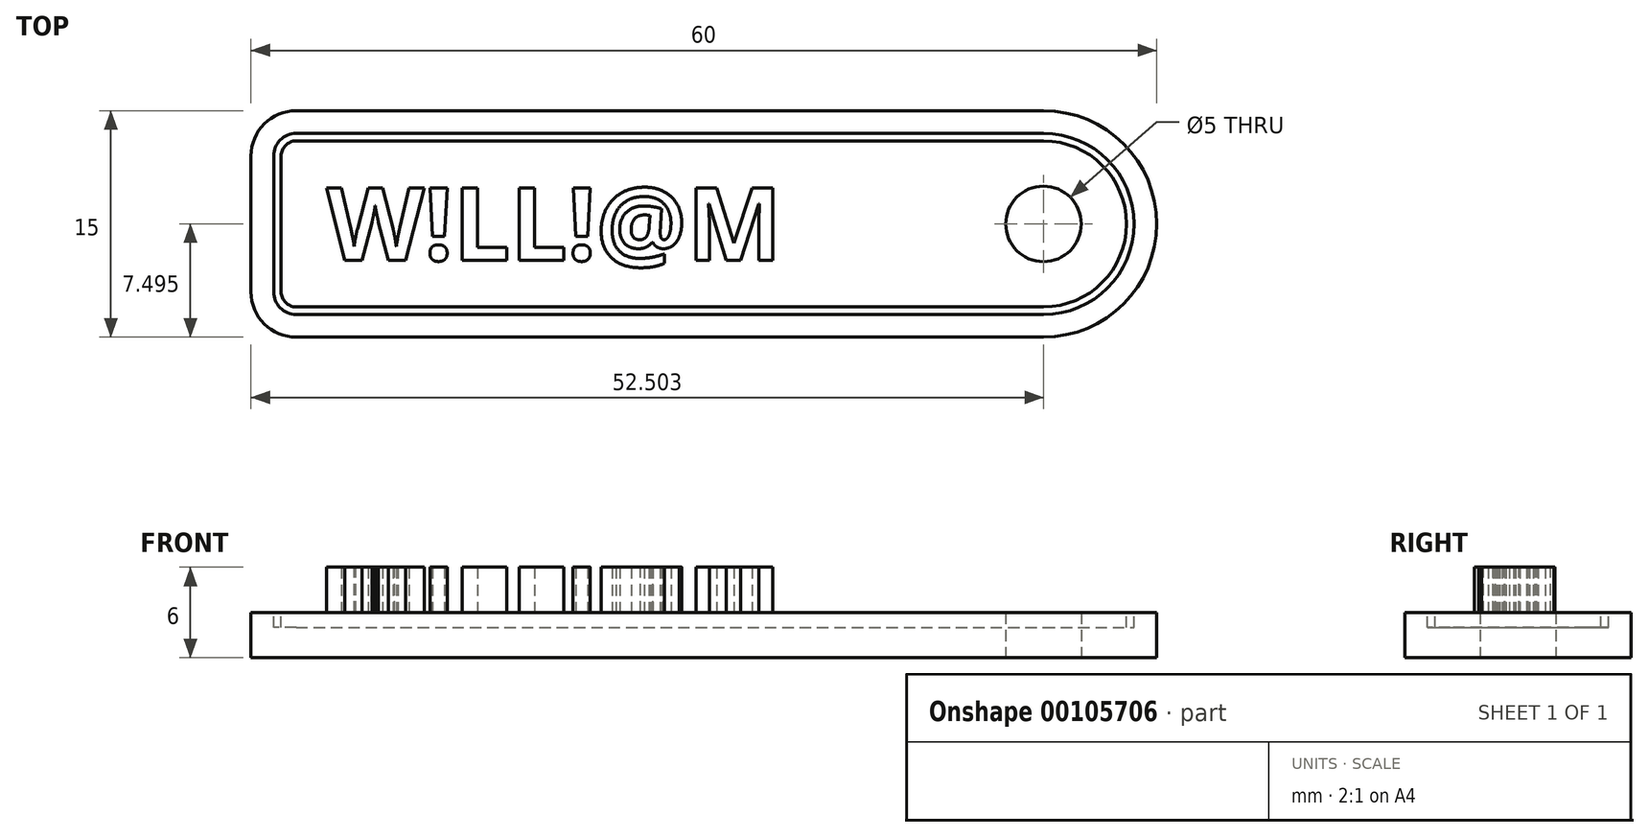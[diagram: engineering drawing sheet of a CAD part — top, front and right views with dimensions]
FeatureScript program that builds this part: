
annotation { "Feature Type Name" : "Feature", "Feature Type Description" : "" }
export const myFeature = defineFeature(function(context is Context, id is Id, definition is map)
    precondition{}
    {
        {
            var Q0;
            Q0=qCreatedBy(makeId("Top.planeOp"),FACE);
            var sketch = newSketch(context, id + "F0", { "sketchPlane" : qUnion([Q0])});
            skLineSegment(sketch, "E0.bottom", {"start": v(-1.37, 15.2) * mm, "end": v(48.13, 15.2) * mm});
            skLineSegment(sketch, "E0.top", {"start": v(-1.37, 0.2) * mm, "end": v(48.13, 0.2) * mm});
            skLineSegment(sketch, "E0.left", {"start": v(-4.37, 12.2) * mm, "end": v(-4.37, 3.2) * mm});
            skPoint(sketch, "E1.visualSharp", {"position": v(-4.37, 15.2) * mm});
            skArc(sketch, "E1.filletArc", {"start": v(-1.37, 15.2) * mm, "mid": v(-3.49, 14.32) * mm, "end": v(-4.37, 12.2) * mm});
            skPoint(sketch, "E2.visualSharp", {"position": v(-4.37, 0.2) * mm});
            skArc(sketch, "E2.filletArc", {"start": v(-4.37, 3.2) * mm, "mid": v(-3.49, 1.07) * mm, "end": v(-1.37, 0.2) * mm});
            skPoint(sketch, "E3.visualSharp", {"position": v(51.13, 0.2) * mm});
            skPoint(sketch, "E4.visualSharp", {"position": v(51.13, 15.2) * mm});
            skArc(sketch, "E5", {"start": v(48.13, 15.2) * mm, "mid": v(55.63, 7.7) * mm, "end": v(48.13, 0.2) * mm});
            skCircle(sketch, "E6", {"center": v(48.13, 7.7) * mm, "radius": 2.5 * mm});
            skSolve(sketch);
        }
        {
            var Q0;
            Q0=makeQuery(id+"F0.imprint","IMPRINT",FACE,{"disambiguationData":[TD([[makeQuery(id+"F0.imprint","IMPRINT",EDGE,{"derivedFrom":sQuery(id+"F0.wireOp",EDGE,"E0.bottom")}),-1.0]])]});
            extrude(context, id + "F1", {"entities" : qUnion([Q0]), "depth" : 3 * mm});
        }
        {
            var Q0;
            Q0=makeQuery(id+"F1.opExtrude","CAP_FACE",FACE,{"disambiguationData":[OSD([sQuery(id+"F0.wireOp",EDGE,"E0.bottom"),sQuery(id+"F0.wireOp",EDGE,"E0.top"),sQuery(id+"F0.wireOp",EDGE,"E0.left"),sQuery(id+"F0.wireOp",EDGE,"E1.filletArc"),sQuery(id+"F0.wireOp",EDGE,"E2.filletArc"),sQuery(id+"F0.wireOp",EDGE,"E5"),sQuery(id+"F0.wireOp",EDGE,"E6")])],"isStart":false});
            var sketch = newSketch(context, id + "F2", { "sketchPlane" : qUnion([Q0])});
            skText(sketch, "E7", { "text": "W!LL!@M", "fontName": "OpenSans-Bold.ttf"});
            skLineSegment(sketch, "E8", {"start": v(55.63, 7.7) * mm, "end": v(-4.37, 7.7) * mm, "construction": true});
            const initialGuessF2  = {"E7": [0.00063, 0.00529, 1, 0, 0.00482]};
            skSetInitialGuess(sketch, initialGuessF2);
            skSolve(sketch);
        }
        {
            var Q0;
            Q0 = qSketchRegion(id + "F2", true);
            extrude(context, id + "F3", {"entities" : qUnion([Q0]), "operationType" : NewBodyOperationType.ADD, "depth" : 3 * mm});
        }
        {
            var Q0;
            {var subQ0=sQuery(id+"F0.wireOp",EDGE,"E6");var subQ1=sQuery(id+"F0.wireOp",EDGE,"E0.left");var subQ2=sQuery(id+"F0.wireOp",EDGE,"E5");var subQ3=sQuery(id+"F0.wireOp",EDGE,"E0.bottom");var subQ4=sQuery(id+"F0.wireOp",EDGE,"E1.filletArc");var subQ5=sQuery(id+"F0.wireOp",EDGE,"E0.top");var subQ6=sQuery(id+"F0.wireOp",EDGE,"E2.filletArc");Q0=makeQuery(id+"F3.boolean.opBoolean","SPLIT",FACE,{"disambiguationData":[TD([makeQuery(id+"F1.opExtrude","SWEPT_FACE",FACE,{"disambiguationData":[OSD([subQ3])]})])],"derivedFrom":makeQuery(id+"F1.opExtrude","CAP_FACE",FACE,{"disambiguationData":[OSD([subQ3,subQ5,subQ1,subQ4,subQ6,subQ2,subQ0])],"isStart":false})});}
            var sketch = newSketch(context, id + "F4", { "sketchPlane" : qUnion([Q0])});
            skArc(sketch, "E9.0", {"start": v(-1.37, 13.7) * mm, "mid": v(-2.43, 13.26) * mm, "end": v(-2.87, 12.2) * mm});
            skArc(sketch, "E9.1", {"start": v(48.13, 13.7) * mm, "mid": v(54.13, 7.7) * mm, "end": v(48.13, 1.7) * mm});
            skLineSegment(sketch, "E9.2", {"start": v(-1.37, 1.7) * mm, "end": v(48.13, 1.7) * mm});
            skLineSegment(sketch, "E9.3", {"start": v(-1.37, 13.7) * mm, "end": v(48.13, 13.7) * mm});
            skArc(sketch, "E9.4", {"start": v(-2.87, 3.2) * mm, "mid": v(-2.43, 2.13) * mm, "end": v(-1.37, 1.7) * mm});
            skLineSegment(sketch, "E9.5", {"start": v(-2.87, 12.2) * mm, "end": v(-2.87, 3.2) * mm});
            skArc(sketch, "E10.0", {"start": v(-1.37, 13.2) * mm, "mid": v(-2.07, 12.9) * mm, "end": v(-2.37, 12.2) * mm});
            skArc(sketch, "E10.1", {"start": v(48.13, 13.2) * mm, "mid": v(53.63, 7.7) * mm, "end": v(48.13, 2.2) * mm});
            skLineSegment(sketch, "E10.2", {"start": v(-1.37, 2.2) * mm, "end": v(48.13, 2.2) * mm});
            skLineSegment(sketch, "E10.3", {"start": v(-1.37, 13.2) * mm, "end": v(48.13, 13.2) * mm});
            skArc(sketch, "E10.4", {"start": v(-2.37, 3.2) * mm, "mid": v(-2.07, 2.49) * mm, "end": v(-1.37, 2.2) * mm});
            skLineSegment(sketch, "E10.5", {"start": v(-2.37, 12.2) * mm, "end": v(-2.37, 3.2) * mm});
            skSolve(sketch);
        }
        {
            var Q0;
            Q0=makeQuery(id+"F4.imprint","IMPRINT",FACE,{"disambiguationData":[TD([[makeQuery(id+"F4.imprint","IMPRINT",EDGE,{"derivedFrom":sQuery(id+"F4.wireOp",EDGE,"E9.0")}),1.0]])]});
            extrude(context, id + "F5", {"entities" : qUnion([Q0]), "operationType" : NewBodyOperationType.REMOVE, "oppositeDirection" : true, "depth" : 1 * mm});
        }
    });
